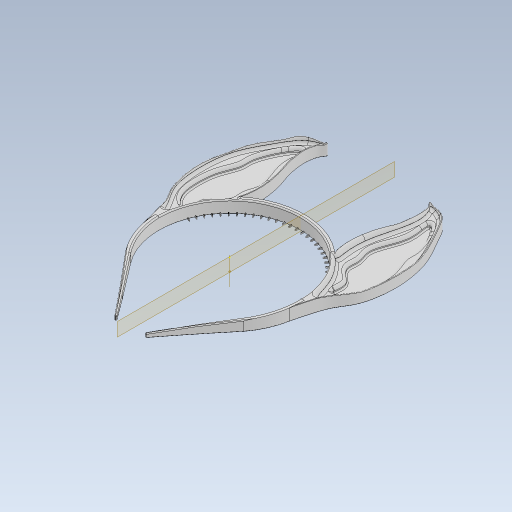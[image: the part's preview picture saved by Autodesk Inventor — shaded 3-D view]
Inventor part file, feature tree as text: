
AUTODESK INVENTOR PART (.ipt)
format: ipt  version: 2023 (Build 270158030, 158C)  size: 2,373,632 bytes
history: native  units: in
note: dims shown in document units (in); Inventor stores cm internally (conversion verified against a paired STEP export)
features: fillet x21, extrude x12, sketch x12, projected_geometry x5, chamfer x2, other x1, pattern_circular x1, mirror x1
ambient origin geometry x8: Origin, YZ Plane, XZ Plane, XY Plane, X Axis, Y Axis, Z Axis, Center Point
bodies: Solid1 (feature_tree), Solid2 (feature_tree)
feature tree (55):
  extrude  "Extrusion1"  TaperAngle=0.0deg  [1 undecoded]
  extrude  "Extrusion2"  Depth=2.2638in
  fillet  "Fillet2"  Radius=0.1181in
  other  "Work Axis1"
  pattern_circular  "Circular Pattern1"  Count=30  [1 undecoded]
  extrude  "Extrusion3"  Depth=3.1496in
  extrude  "Extrusion4"  Depth=0.3937in
  fillet  "Fillet5"  Radius=0.0427in
  fillet  "Fillet6"  Radius=59.0551in
  fillet  "Fillet7"  Radius=59.0551in
  fillet  "Fillet8"  Radius=0.3937in
  extrude  "Extrusion10"  Depth=0.3937in
  extrude  "Extrusion11"  Depth=0.3937in
  extrude  "Extrusion12"  Depth=0.3937in
  sketch  "Sketch17"  dims[d75=0.1181in d76=4.3307in d77=25.1969in d78=0.7087in d79=4.3307in d80=0.3937in d81=0.0in d82=0.0in d85=0.0248in d86=0.0394in d87=0.0394in d88=0.0236in d104=0.3937in d105=0.0in d107=0.315in d108=0.0in d121=0.0591in d122=0.0591in d123=1.378in d125=0.3346in d126=0.0in d130=2.3495in d131=2.2052in d132=2.0826in d133=1.4138in d134=2.5284in d135=1.4901in d136=2.1896in d137=2.5146in d138=2.7368in d139=1.4623in d140=0.488in d141=0.3104in d142=0.2859in d143=0.2088in d144=0.2171in d145=0.23in d147=0.2362in d148=0.0787in d149=0.0787in d150=0.0394in d153=0.0394in d154=0.1181in d155=0.0787in d156=0.0787in d158=23.622in d159=1.9685in d161=7.8078in d162=2.3622in d163=0.7874in d164=0.9817in d165=0.0in d166=0.0in d167=0.0787in d168=0.1969in d169=0.1969in d170=0.1181in d171=0.0197in d172=0.0079in d173=0.0394in d174=0.0197in d175=0.0197in d182=0.0984in d183=0.0394in d184=0.0984in d185=0.0394in d186=0.0591in d187=0.0394in d188=0.0197in d189=0.076in d190=0.0in d191=0.0in d192=0.0079in d193=0.0197in d194=0.0787in d195=45.0deg d196=0.0in d197=0.0in d199=0.3937in d200=0.0in d201=0.3543in d202=0.0in d203=0.315in d205=0.1969in d206=0.0in d207=0.1181in d208=0.1181in d209=0.0118in d210=0.0748in d211=0.0866in d212=0.0394in d213=0.015in d214=0.0787in d215=45.0deg]
  fillet  "Fillet31"  Radius=4.3307in
  fillet  "Fillet32"  Radius=0.3937in
  fillet  "Fillet33"  [1 undecoded]
  fillet  "Fillet34"  Radius=0.0248in
  fillet  "Fillet35"  Radius=0.0394in
  chamfer  "Chamfer2"  Distance=0.0394in
  mirror  "Mirror1"
  fillet  "Fillet30"  Radius=0.0236in
  fillet  "Fillet28"  Radius=0.3937in
  fillet  "Fillet19"  Radius=0.315in
  extrude  "Extrusion5"  Depth=0.3937in
  extrude  "Extrusion7"  Depth=0.3937in
  extrude  "Extrusion6"  Depth=0.3937in
  fillet  "Fillet20"  Radius=0.3346in
  fillet  "Fillet21"  Radius=2.3495in
  fillet  "Fillet22"  Radius=2.2052in
  fillet  "Fillet23"  Radius=2.0826in
  fillet  "Fillet24"  Radius=1.4138in
  fillet  "Fillet25"  Radius=2.5284in
  fillet  "Fillet26"  Radius=1.4901in
  extrude  "Extrusion8"  Depth=0.3937in
  fillet  "Fillet27"  Radius=2.5146in
  extrude  "Extrusion9"  Depth=0.3937in
  chamfer  "Chamfer1"  Distance=1.4623in
  sketch  "Sketch2"  dims[d18=0.0in d19=0.0in]
  sketch  "Sketch5"  dims[d20=0.0in d23=2.2638in d25=0.1181in]
  sketch  "Sketch6"  dims[d26=0.1181in]
  sketch  "Sketch7"  dims[d27=0.1181in]
  sketch  "Sketch8"  dims[d30=0.3937in d31=0.0in]
  sketch  "Sketch9"  dims[d48=0.0433in d49=0.0in]
  sketch  "Sketch11"  dims[d50=0.0118in]
  sketch  "Sketch12"  dims[d57=0.0787in d58=0.0157in d59=0.7594in]
  projected_geometry  "Projected Loop1"
  sketch  "Sketch13"  dims[d60=2.1102in d61=11.811in d62=-0.962in]
  projected_geometry  "Projected Loop2"
  projected_geometry  "Projected Loop3"
  sketch  "Sketch14"  dims[d64=0.889in d65=3.1496in]
  projected_geometry  "Projected Loop4"
  sketch  "Sketch16"  dims[d68=0.0394in d69=0.0118in d70=0.0427in d71=59.0551in d72=59.0551in d73=0.3937in d74=0.0in]
  projected_geometry  "Projected Loop5"
note: 3 required parameter values undecoded (feature->parameter linkage not recoverable at this tier; creation-order binding heuristic only, values carry confidence <= 0.55)
